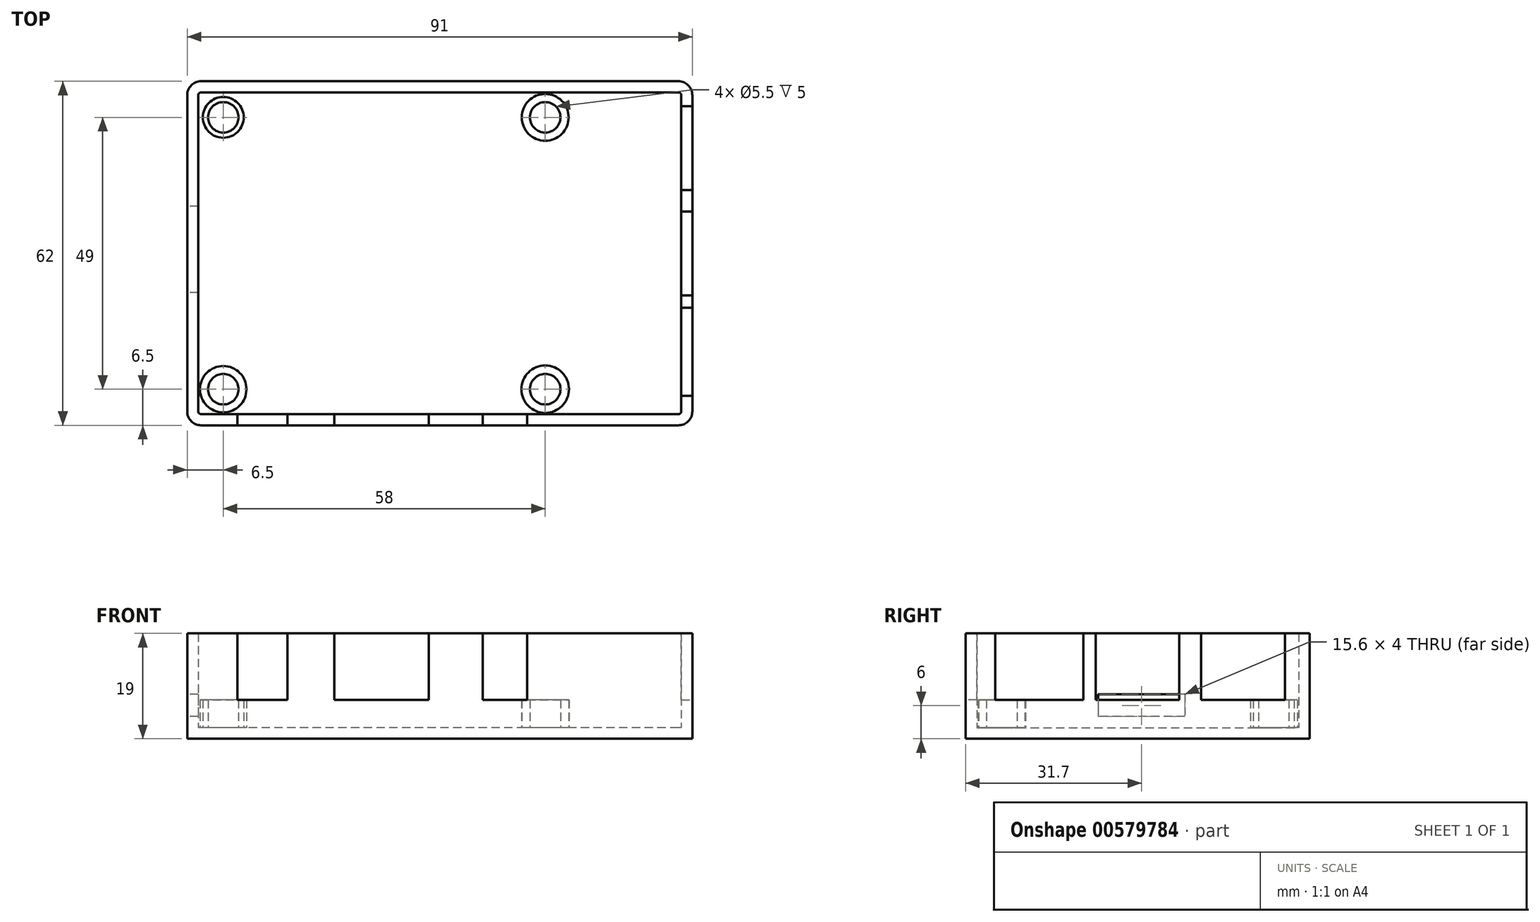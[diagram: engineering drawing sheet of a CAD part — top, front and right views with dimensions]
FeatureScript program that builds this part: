
annotation { "Feature Type Name" : "Feature", "Feature Type Description" : "" }
export const myFeature = defineFeature(function(context is Context, id is Id, definition is map)
    precondition{}
    {
        {
            var Q0;
            Q0=qCreatedBy(makeId("Top.planeOp"),FACE);
            var sketch = newSketch(context, id + "F0", { "sketchPlane" : qUnion([Q0])});
            skLineSegment(sketch, "E0.bottom", {"start": v(2.5, 0) * mm, "end": v(88.5, 0) * mm});
            skLineSegment(sketch, "E0.top", {"start": v(2.5, -62) * mm, "end": v(88.5, -62) * mm});
            skLineSegment(sketch, "E0.left", {"start": v(0, -2.5) * mm, "end": v(0, -59.5) * mm});
            skLineSegment(sketch, "E0.right", {"start": v(91, -2.5) * mm, "end": v(91, -59.5) * mm});
            skPoint(sketch, "E1.visualSharp", {"position": v(0, 0) * mm});
            skArc(sketch, "E1.filletArc", {"start": v(2.5, 0) * mm, "mid": v(0.73, -0.73) * mm, "end": v(0, -2.5) * mm});
            skPoint(sketch, "E2.visualSharp", {"position": v(91, 0) * mm});
            skArc(sketch, "E2.filletArc", {"start": v(91, -2.5) * mm, "mid": v(90.27, -0.73) * mm, "end": v(88.5, 0) * mm});
            skPoint(sketch, "E3.visualSharp", {"position": v(91, -62) * mm});
            skArc(sketch, "E3.filletArc", {"start": v(88.5, -62) * mm, "mid": v(90.27, -61.27) * mm, "end": v(91, -59.5) * mm});
            skPoint(sketch, "E4.visualSharp", {"position": v(0, -62) * mm});
            skArc(sketch, "E4.filletArc", {"start": v(0, -59.5) * mm, "mid": v(0.73, -61.27) * mm, "end": v(2.5, -62) * mm});
            skLineSegment(sketch, "E5.0", {"start": v(2.5, -2) * mm, "end": v(88.5, -2) * mm});
            skArc(sketch, "E5.1", {"start": v(89, -2.5) * mm, "mid": v(88.85, -2.15) * mm, "end": v(88.5, -2) * mm});
            skArc(sketch, "E5.2", {"start": v(2.5, -2) * mm, "mid": v(2.15, -2.15) * mm, "end": v(2, -2.5) * mm});
            skLineSegment(sketch, "E5.3", {"start": v(89, -2.5) * mm, "end": v(89, -59.5) * mm});
            skLineSegment(sketch, "E5.4", {"start": v(2, -2.5) * mm, "end": v(2, -59.5) * mm});
            skArc(sketch, "E5.5", {"start": v(2, -59.5) * mm, "mid": v(2.15, -59.85) * mm, "end": v(2.5, -60) * mm});
            skLineSegment(sketch, "E5.6", {"start": v(2.5, -60) * mm, "end": v(88.5, -60) * mm});
            skArc(sketch, "E5.7", {"start": v(88.5, -60) * mm, "mid": v(88.85, -59.85) * mm, "end": v(89, -59.5) * mm});
            skSolve(sketch);
        }
        {
            var Q0;
            Q0=makeQuery(id+"F0.imprint","IMPRINT",FACE,{"disambiguationData":[TD([[makeQuery(id+"F0.imprint","IMPRINT",EDGE,{"derivedFrom":sQuery(id+"F0.wireOp",EDGE,"E0.bottom")}),-1.0]])]});
            var Q1;
            Q1=makeQuery(id+"F0.imprint","IMPRINT",FACE,{"disambiguationData":[TD([[makeQuery(id+"F0.imprint","IMPRINT",EDGE,{"derivedFrom":sQuery(id+"F0.wireOp",EDGE,"E5.0")}),-1.0]])]});
            extrude(context, id + "F1", {"entities" : qUnion([Q0, Q1]), "depth" : 2 * mm, "offsetDistance" : 25 * mm});
        }
        {
            var Q0;
            Q0 = qSketchRegion(id + "F0", true);
            extrude(context, id + "F2", {"entities" : qUnion([Q0]), "operationType" : NewBodyOperationType.ADD, "depth" : 19 * mm, "offsetDistance" : 25 * mm});
        }
        {
            var Q0;
            Q0=makeQuery(id+"F1.opExtrude","CAP_FACE",FACE,{"disambiguationData":[OSD([sQuery(id+"F0.wireOp",EDGE,"E0.bottom"),sQuery(id+"F0.wireOp",EDGE,"E0.top"),sQuery(id+"F0.wireOp",EDGE,"E0.left"),sQuery(id+"F0.wireOp",EDGE,"E0.right"),sQuery(id+"F0.wireOp",EDGE,"E1.filletArc"),sQuery(id+"F0.wireOp",EDGE,"E2.filletArc"),sQuery(id+"F0.wireOp",EDGE,"E3.filletArc"),sQuery(id+"F0.wireOp",EDGE,"E4.filletArc")])],"isStart":false});
            var sketch = newSketch(context, id + "F3", { "sketchPlane" : qUnion([Q0])});
            skCircle(sketch, "E6", {"center": v(6.5, -6.5) * mm, "radius": 2.75 * mm});
            skCircle(sketch, "E7", {"center": v(6.5, -55.5) * mm, "radius": 2.75 * mm});
            skCircle(sketch, "E8", {"center": v(64.5, -55.5) * mm, "radius": 2.75 * mm});
            skCircle(sketch, "E9", {"center": v(64.5, -6.5) * mm, "radius": 2.75 * mm});
            skCircle(sketch, "E10", {"center": v(6.5, -6.5) * mm, "radius": 3.68 * mm});
            skCircle(sketch, "E11", {"center": v(64.5, -6.5) * mm, "radius": 4.22 * mm});
            skCircle(sketch, "E12", {"center": v(6.5, -55.5) * mm, "radius": 4.18 * mm});
            skCircle(sketch, "E13", {"center": v(64.5, -55.5) * mm, "radius": 4.28 * mm});
            skSolve(sketch);
        }
        {
            var Q0;
            Q0 = qSketchRegion(id + "F3", true);
            extrude(context, id + "F4", {"entities" : qUnion([Q0]), "operationType" : NewBodyOperationType.ADD, "depth" : 5 * mm, "offsetDistance" : 25 * mm});
        }
        {
            var Q0;
            Q0=makeQuery(id+"F2.opExtrude","CAP_FACE",FACE,{"disambiguationData":[OSD([sQuery(id+"F0.wireOp",EDGE,"E0.bottom"),sQuery(id+"F0.wireOp",EDGE,"E0.top"),sQuery(id+"F0.wireOp",EDGE,"E0.left"),sQuery(id+"F0.wireOp",EDGE,"E0.right"),sQuery(id+"F0.wireOp",EDGE,"E1.filletArc"),sQuery(id+"F0.wireOp",EDGE,"E2.filletArc"),sQuery(id+"F0.wireOp",EDGE,"E3.filletArc"),sQuery(id+"F0.wireOp",EDGE,"E4.filletArc"),sQuery(id+"F0.wireOp",EDGE,"E5.0"),sQuery(id+"F0.wireOp",EDGE,"E5.1"),sQuery(id+"F0.wireOp",EDGE,"E5.2"),sQuery(id+"F0.wireOp",EDGE,"E5.3"),sQuery(id+"F0.wireOp",EDGE,"E5.4"),sQuery(id+"F0.wireOp",EDGE,"E5.5"),sQuery(id+"F0.wireOp",EDGE,"E5.6"),sQuery(id+"F0.wireOp",EDGE,"E5.7")])],"isStart":false});
            var sketch = newSketch(context, id + "F5", { "sketchPlane" : qUnion([Q0])});
            skLineSegment(sketch, "E14.bottom", {"start": v(91, -4.5) * mm, "end": v(89, -4.5) * mm});
            skLineSegment(sketch, "E14.top", {"start": v(91, -19.6) * mm, "end": v(89, -19.6) * mm});
            skLineSegment(sketch, "E14.left", {"start": v(91, -4.5) * mm, "end": v(91, -19.6) * mm});
            skLineSegment(sketch, "E14.right", {"start": v(89, -4.5) * mm, "end": v(89, -19.6) * mm});
            skLineSegment(sketch, "E15.bottom", {"start": v(89, -23.5) * mm, "end": v(91, -23.5) * mm});
            skLineSegment(sketch, "E15.top", {"start": v(89, -38.6) * mm, "end": v(91, -38.6) * mm});
            skLineSegment(sketch, "E15.left", {"start": v(89, -23.5) * mm, "end": v(89, -38.6) * mm});
            skLineSegment(sketch, "E15.right", {"start": v(91, -23.5) * mm, "end": v(91, -38.6) * mm});
            skLineSegment(sketch, "E16.bottom", {"start": v(89, -40.8) * mm, "end": v(91, -40.8) * mm});
            skLineSegment(sketch, "E16.top", {"start": v(89, -56.7) * mm, "end": v(91, -56.7) * mm});
            skLineSegment(sketch, "E16.left", {"start": v(89, -40.8) * mm, "end": v(89, -56.7) * mm});
            skLineSegment(sketch, "E16.right", {"start": v(91, -40.8) * mm, "end": v(91, -56.7) * mm});
            skLineSegment(sketch, "E17.bottom", {"start": v(9.05, -60) * mm, "end": v(18.05, -60) * mm});
            skLineSegment(sketch, "E17.top", {"start": v(9.05, -62) * mm, "end": v(18.05, -62) * mm});
            skLineSegment(sketch, "E17.left", {"start": v(9.05, -60) * mm, "end": v(9.05, -62) * mm});
            skLineSegment(sketch, "E17.right", {"start": v(18.05, -60) * mm, "end": v(18.05, -62) * mm});
            skLineSegment(sketch, "E18.bottom", {"start": v(26.5, -60) * mm, "end": v(43.5, -60) * mm});
            skLineSegment(sketch, "E18.top", {"start": v(26.5, -62) * mm, "end": v(43.5, -62) * mm});
            skLineSegment(sketch, "E18.left", {"start": v(26.5, -60) * mm, "end": v(26.5, -62) * mm});
            skLineSegment(sketch, "E18.right", {"start": v(43.5, -60) * mm, "end": v(43.5, -62) * mm});
            skLineSegment(sketch, "E19.bottom", {"start": v(53.25, -60) * mm, "end": v(61.25, -60) * mm});
            skLineSegment(sketch, "E19.top", {"start": v(53.25, -62) * mm, "end": v(61.25, -62) * mm});
            skLineSegment(sketch, "E19.left", {"start": v(53.25, -60) * mm, "end": v(53.25, -62) * mm});
            skLineSegment(sketch, "E19.right", {"start": v(61.25, -60) * mm, "end": v(61.25, -62) * mm});
            skSolve(sketch);
        }
        {
            var Q0;
            Q0 = qSketchRegion(id + "F5", true);
            extrude(context, id + "F6", {"entities" : qUnion([Q0]), "operationType" : NewBodyOperationType.REMOVE, "oppositeDirection" : true, "depth" : 12 * mm, "offsetDistance" : 25 * mm});
        }
        {
            var Q0;
            {var subQ0=sQuery(id+"F0.wireOp",EDGE,"E0.left");Q0=makeQuery(id+"F2.boolean.opBoolean","MERGE",FACE,{"derivedFrom":[makeQuery(id+"F1.opExtrude","SWEPT_FACE",FACE,{"disambiguationData":[OSD([subQ0])]}),makeQuery(id+"F2.opExtrude","SWEPT_FACE",FACE,{"disambiguationData":[OSD([subQ0])]})]});}
            var sketch = newSketch(context, id + "F7", { "sketchPlane" : qUnion([Q0])});
            skLineSegment(sketch, "E20.bottom", {"start": v(22.5, 8) * mm, "end": v(38.1, 8) * mm});
            skLineSegment(sketch, "E20.top", {"start": v(22.5, 4) * mm, "end": v(38.1, 4) * mm});
            skLineSegment(sketch, "E20.left", {"start": v(22.5, 8) * mm, "end": v(22.5, 4) * mm});
            skLineSegment(sketch, "E20.right", {"start": v(38.1, 8) * mm, "end": v(38.1, 4) * mm});
            skSolve(sketch);
        }
        {
            var Q0;
            Q0 = qSketchRegion(id + "F7", true);
            extrude(context, id + "F8", {"entities" : qUnion([Q0]), "operationType" : NewBodyOperationType.REMOVE, "oppositeDirection" : true, "depth" : 2 * mm, "offsetDistance" : 25 * mm});
        }
    });
